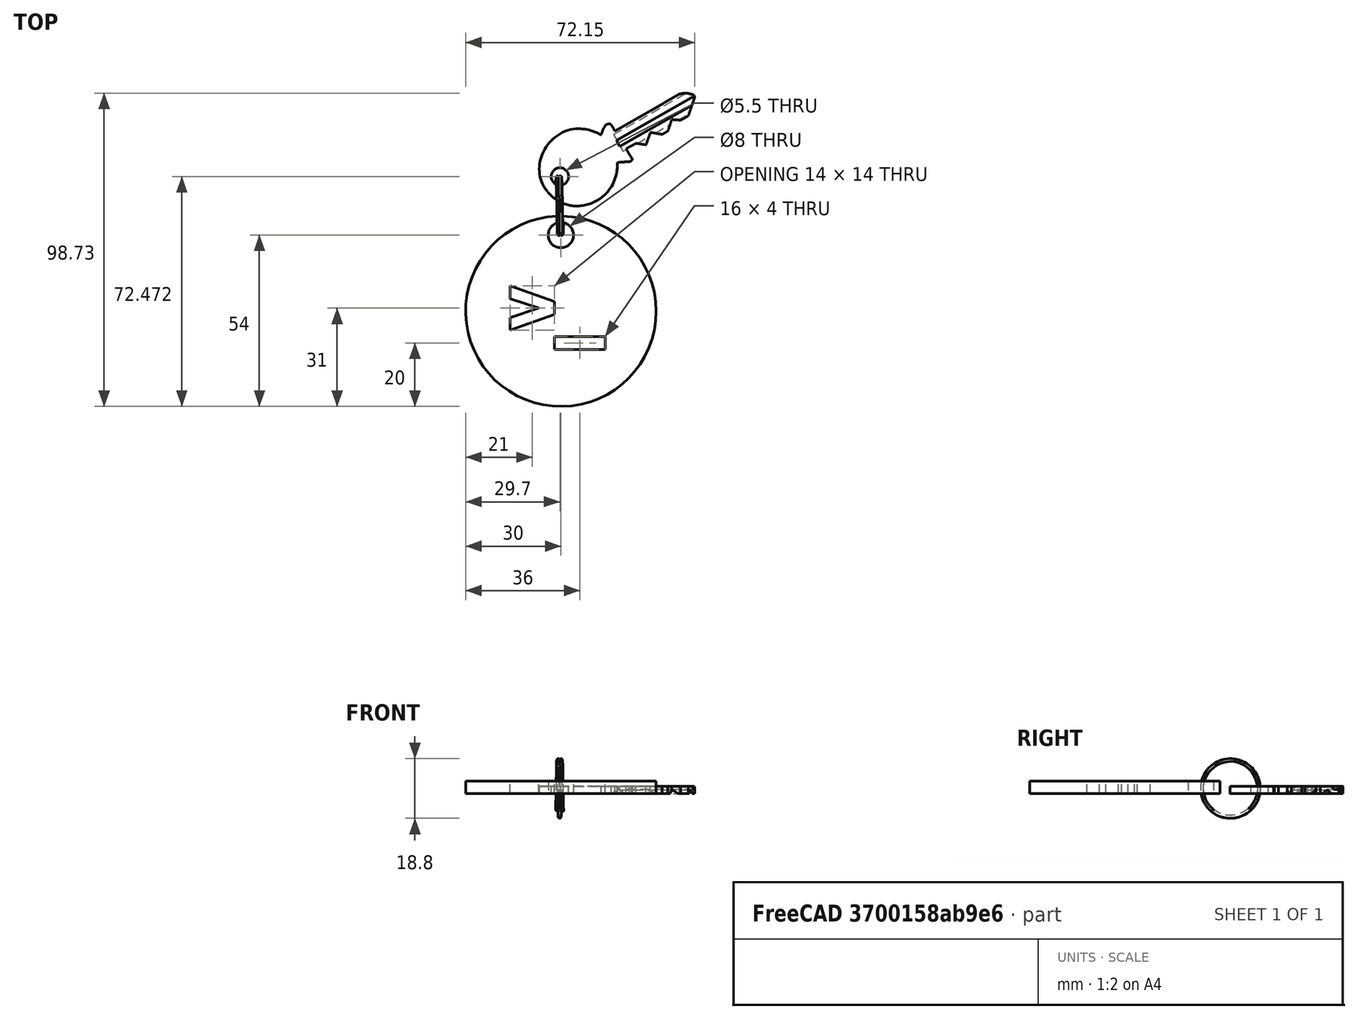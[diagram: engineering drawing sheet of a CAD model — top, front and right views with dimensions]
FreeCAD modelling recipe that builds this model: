
FCSTD DOCUMENT  (FreeCAD 0.17R13509 (Git))
Label: Terminal
License: CreativeCommons Attribution-ShareAlike
LicenseURL: http://creativecommons.org/licenses/by-sa/4.0/
objects: Part::Feature×2, Sketcher::SketchObject×1, PartDesign::Pad×1, App::DocumentObjectGroup×1
note: 5 computed .brp shape members not serialized (recipe doc carries the construction recipe); baked Part::Feature solids carry a one-line shape summary decoded from their .brp

FEATURE [Part::Feature] Sweep  label="key-ring-model-1"
  Placement = pos=(-1.2,30.2546,1.6391) rot=(0.333333,0.881918,0.333333;1.69612rad)
  shape: bbox 3.31 x 27.02 x 26.33 mm, 4 faces (baked)
FEATURE [Part::Feature] Cut  label="key-model-1"
  Placement = pos=(-5.46976,36.5266,0) rot=(0,0,1;0.517888rad)
  shape: bbox 49.82 x 36.6 x 2.3 mm, 44 faces (baked)
FEATURE [Sketcher::SketchObject] Sketch001
  MapMode = 5
  Placement = pos=(-30,-33,0) rot=(0,0,1;0rad)
  sketch-geometry (16):
    g0: Circle CenterX=30 CenterY=30 CenterZ=0 NormalX=0 NormalY=0 NormalZ=1 AngleXU=0 Radius=30
    g1: LineSegment StartX=28 StartY=22 StartZ=0 EndX=44 EndY=22 EndZ=0
    g2: LineSegment StartX=44 StartY=22 StartZ=0 EndX=44 EndY=18 EndZ=0
    g3: LineSegment StartX=44 StartY=18 StartZ=0 EndX=28 EndY=18 EndZ=0
    g4: LineSegment StartX=28 StartY=18 StartZ=0 EndX=28 EndY=22 EndZ=0
    g5: LineSegment StartX=14 StartY=38 StartZ=0 EndX=28 EndY=33 EndZ=0
    g6: LineSegment StartX=28 StartY=33 StartZ=0 EndX=28 EndY=29 EndZ=0
    g7: LineSegment StartX=28 StartY=29 StartZ=0 EndX=14 EndY=24 EndZ=0
    g8: LineSegment StartX=14 StartY=24 StartZ=0 EndX=14 EndY=28 EndZ=0
    g9: LineSegment StartX=14 StartY=28 StartZ=0 EndX=23 EndY=31 EndZ=0
    g10: LineSegment StartX=23 StartY=31 StartZ=0 EndX=14 EndY=34 EndZ=0
    g11: LineSegment StartX=14 StartY=34 StartZ=0 EndX=14 EndY=38 EndZ=0
    g12: LineSegment [constr] StartX=14 StartY=34 StartZ=0 EndX=14 EndY=28 EndZ=0
    g13: LineSegment [constr] StartX=23 StartY=31 StartZ=0 EndX=28 EndY=31 EndZ=0
    g14: Circle CenterX=30 CenterY=54 CenterZ=0 NormalX=0 NormalY=0 NormalZ=1 AngleXU=0 Radius=4
    g15: LineSegment [constr] StartX=30 StartY=54 StartZ=0 EndX=30 EndY=30 EndZ=0
  constraints (45):
    c: Tangent(g-1,g0)
    c: Tangent(g0,g-2)
    c: Radius(g0) = 30
    c: Coincident(g1,g2)
    c: Coincident(g2,g3)
    c: Coincident(g3,g4)
    c: Coincident(g4,g1)
    c: Horizontal(g1)
    c: Horizontal(g3)
    c: Vertical(g2)
    c: Vertical(g4)
    c: DistanceY(g-1,g3) = 18
    c: DistanceX(g-1,g3) = 28
    c: DistanceX(g1,g1) = 16
    c: DistanceY(g2,g2) = 4
    c: Coincident(g5,g6)
    c: Vertical(g6)
    c: Coincident(g6,g7)
    c: Coincident(g7,g8)
    c: Vertical(g8)
    c: Coincident(g8,g9)
    c: Coincident(g9,g10)
    c: Coincident(g10,g11)
    c: Coincident(g11,g5)
    c: Vertical(g11)
    c: Coincident(g12,g8)
    c: Coincident(g12,g10)
    c: Vertical(g12)
    c: DistanceX(g5,g9) = 9
    c: Distance(g5,g11) = 14
    c: DistanceX(g-1,g7) = 14
    c: Coincident(g9,g13)
    c: PointOnObject(g13,g6)
    c: Symmetric(g5,g6,g13)
    c: DistanceY(g-1,g9) = 31
    c: DistanceY(g6,g6) = 4
    c: Symmetric(g5,g7,g13)
    c: Equal(g8,g6)
    c: DistanceY(g8,g10) = 6
    c: Equal(g11,g8)
    c: Coincident(g15,g14)
    c: Coincident(g15,g0)
    c: Vertical(g15)
    c: Radius(g14) = 4
    c: DistanceY(g15,g15) = 24
FEATURE [PartDesign::Pad] Pad
  Length = 4
  Length2 = 100
  Placement = pos=(-30,-33,0) rot=(0,0,1;0rad)
  Profile = -> Sketch001
  Refine = true
  Type = 0
FEATURE [App::DocumentObjectGroup] Group  label="Assembly"
  Group = -> [Sweep,Cut,Pad]
